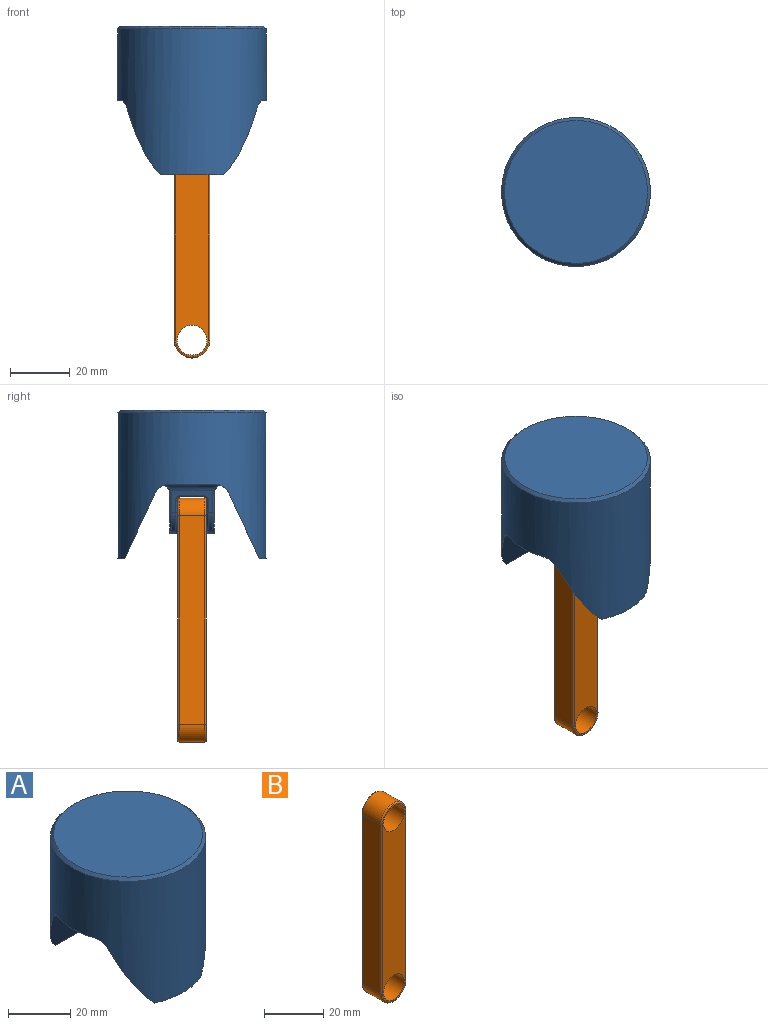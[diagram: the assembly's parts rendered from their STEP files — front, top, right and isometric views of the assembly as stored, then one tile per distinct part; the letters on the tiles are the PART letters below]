
ASSEMBLY  parts=2 mates=1
PART A: 54 faces, bbox 50x50x50 mm
  f0: plane 14.31x7.44mm, normal (-0.96,0,-0.29), area 44.3mm2, adj f1,f15,f22,f35,f36,f37,f38,f39
  f1: cylinder r=10mm len=19.11mm, axis (0,1,0), area 38.2mm2, adj f0,f2,f34,f43
  f2: plane 14.31x7.44mm, normal (0.96,0,-0.29), area 44.3mm2, adj f1,f15,f19,f28,f29,f30,f31,f32
  f3: cylinder r=5mm len=10mm, axis (0,1,0), area 78.5mm2, adj f18,f27
  f4: plane 15.65x10.28mm, normal (0,0,-1), area 154.5mm2, adj f6,f9,f11,f22
  f5: plane 21.08x2.33mm, normal (0,0,-1), area 33.1mm2, adj f6,f12
  f6: cylinder r=25mm len=50mm, axis (0,0,-1), area 5814.1mm2, adj f4,f5,f8,f9,f10,f11,f12,f13
  f7: plane 48x48mm, normal (0,0,1), area 1809.6mm2, adj f14
  f8: plane 21.08x2.33mm, normal (0,0,-1), area 33.1mm2, adj f6,f13
  f9: cylinder r=5mm len=47.49mm, axis (-1,0,0), area 214.5mm2, adj f4,f6,f10,f12,f19,f21,f22,f40
  f10: plane 15.65x10.28mm, normal (0,0,-1), area 154.5mm2, adj f6,f9,f11,f19
  f11: cylinder r=5mm len=47.49mm, axis (-1,0,0), area 214.5mm2, adj f4,f6,f10,f13,f19,f20,f22,f47
  f12: plane 43.47x22.11mm, normal (0,-0.91,-0.42), area 844.7mm2, adj f5,f6,f9
  f13: plane 43.47x22.11mm, normal (0,0.91,-0.42), area 844.7mm2, adj f6,f8,f11
  f14: cone r=24mm half-angle=45deg, axis (0,0,-1), area 217.7mm2, adj f6,f7
  f15: cylinder r=10mm len=19.11mm, axis (0,1,0), area 38.2mm2, adj f0,f2,f33,f50
  f16: cylinder r=5mm len=10mm, axis (0,1,0), area 78.5mm2, adj f17,f26
  f17: plane 22.11x13.11mm, normal (0,-1,0), area 139.9mm2, adj f16,f20,f49,f50,f51
  f18: plane 22.11x13.11mm, normal (0,1,0), area 139.9mm2, adj f3,f21,f42,f43,f44
  f19: cylinder r=3mm len=18.47mm, axis (0,1,0), area 63.3mm2, adj f2,f9,f10,f11,f40,f47
  f20: cylinder r=3mm len=26.72mm, axis (1,0,0), area 85mm2, adj f11,f17,f47,f48,f52,f53
  f21: cylinder r=3mm len=26.72mm, axis (-1,0,0), area 85mm2, adj f9,f18,f40,f41,f45,f46
  f22: cylinder r=3mm len=18.47mm, axis (0,-1,0), area 63.3mm2, adj f0,f4,f9,f11,f46,f53
  f23: cylinder r=1mm len=21.68mm, axis (-1,0,0), area 33.3mm2, adj f24,f27,f30,f38
  f24: plane 21.68x8mm, normal (0,0,-1), area 173.4mm2, adj f23,f25,f28,f39
  f25: cylinder r=1mm len=21.68mm, axis (-1,0,0), area 33.3mm2, adj f24,f26,f29,f37
  f26: plane 20.76x10.92mm, normal (0,1,0), area 93mm2, adj f16,f25,f31,f33,f35
  f27: plane 20.76x10.92mm, normal (0,-1,0), area 93mm2, adj f3,f23,f32,f34,f36
  f28: cylinder r=0.5mm len=8mm, axis (0,1,0), area 5.1mm2, adj f2,f24,f29,f30
  f29: bspline ~1.76x1.76mm, area 1.3mm2, adj f2,f25,f28,f31
  f30: bspline ~1.76x1.57mm, area 1.3mm2, adj f2,f23,f28,f32
  f31: cylinder r=0.5mm len=4.37mm, axis (0.29,0,0.96), area 3.5mm2, adj f2,f26,f29,f33
  f32: cylinder r=0.5mm len=4.37mm, axis (-0.29,0,-0.96), area 3.5mm2, adj f2,f27,f30,f34
  f33: torus R=9.5mm, axis (0,-1,0), area 19.6mm2, adj f15,f26,f31,f35
  f34: torus R=9.5mm, axis (0,-1,0), area 19.6mm2, adj f1,f27,f32,f36
  f35: cylinder r=0.5mm len=4.37mm, axis (0.29,0,-0.96), area 3.5mm2, adj f0,f26,f33,f37
  f36: cylinder r=0.5mm len=4.37mm, axis (-0.29,0,0.96), area 3.5mm2, adj f0,f27,f34,f38
  f37: bspline ~1.76x1.5mm, area 1.3mm2, adj f0,f25,f35,f39
  f38: bspline ~1.56x1.5mm, area 1.4mm2, adj f0,f23,f36,f39
  f39: cylinder r=0.5mm len=8mm, axis (0,-1,0), area 5.1mm2, adj f0,f24,f37,f38
  f40: bspline ~2.61x2.61mm, area 1.7mm2, adj f9,f19,f21,f41
  f41: bspline ~2.09x1.12mm, area 0.8mm2, adj f2,f21,f40,f42
  f42: cylinder r=0.5mm len=6.56mm, axis (0.29,0,0.96), area 5.3mm2, adj f2,f18,f41,f43
  f43: torus R=9.5mm, axis (0,-1,0), area 19.6mm2, adj f1,f18,f42,f44
  f44: cylinder r=0.5mm len=6.56mm, axis (0.29,0,-0.96), area 5.3mm2, adj f0,f18,f43,f45
  f45: bspline ~2.09x1.12mm, area 0.8mm2, adj f0,f21,f44,f46
  f46: bspline ~2.61x2.61mm, area 1.7mm2, adj f9,f21,f22,f45
  f47: bspline ~2.61x2.61mm, area 1.7mm2, adj f11,f19,f20,f48
  f48: bspline ~2.09x1.12mm, area 0.8mm2, adj f2,f20,f47,f49
  f49: cylinder r=0.5mm len=6.56mm, axis (-0.29,0,-0.96), area 5.3mm2, adj f2,f17,f48,f50
  f50: torus R=9.5mm, axis (0,-1,0), area 19.6mm2, adj f15,f17,f49,f51
  f51: cylinder r=0.5mm len=6.56mm, axis (-0.29,0,0.96), area 5.3mm2, adj f0,f17,f50,f52
  f52: bspline ~2.09x1.12mm, area 0.8mm2, adj f0,f20,f51,f53
  f53: bspline ~2.61x2.61mm, area 1.7mm2, adj f11,f20,f22,f52
PART B: 16 faces, bbox 13x9.5x83 mm
  f0: cylinder r=6mm len=12mm, axis (0,1,0), area 160.2mm2, adj f1,f3,f8,f12
  f1: plane 70x8.5mm, normal (-1,0,0), area 595mm2, adj f0,f2,f9,f13
  f2: cylinder r=6mm len=12mm, axis (0,1,0), area 160.2mm2, adj f1,f3,f11,f15
  f3: plane 70x8.5mm, normal (1,0,0), area 595mm2, adj f0,f2,f10,f14
  f4: cylinder r=5mm len=10mm, axis (0,1,0), area 298.5mm2, adj f6,f7
  f5: cylinder r=5mm len=10mm, axis (0,1,0), area 298.5mm2, adj f6,f7
  f6: plane 81x11mm, normal (0,-1,0), area 708mm2, adj f4,f5,f12,f13,f14,f15
  f7: plane 81x11mm, normal (0,1,0), area 708mm2, adj f4,f5,f8,f9,f10,f11
  f8: torus R=5.5mm, axis (0,-1,0), area 14.4mm2, adj f0,f7,f9,f10
  f9: cylinder r=0.5mm len=70mm, axis (0,0,-1), area 55mm2, adj f1,f7,f8,f11
  f10: cylinder r=0.5mm len=70mm, axis (0,0,1), area 55mm2, adj f3,f7,f8,f11
  f11: torus R=5.5mm, axis (0,-1,0), area 14.4mm2, adj f2,f7,f9,f10
  f12: torus R=5.5mm, axis (0,-1,0), area 14.4mm2, adj f0,f6,f13,f14
  f13: cylinder r=0.5mm len=70mm, axis (0,0,1), area 55mm2, adj f1,f6,f12,f15
  f14: cylinder r=0.5mm len=70mm, axis (0,0,-1), area 55mm2, adj f3,f6,f12,f15
  f15: torus R=5.5mm, axis (0,-1,0), area 14.4mm2, adj f2,f6,f13,f14
PLACE A t=(-25.07,-50.18,-49.96)mm
PLACE B t=(-25.07,-50.18,-49.96)mm
MATE revolute A.f3 <-> B.f0  axis (0,1,0) through (-25.07,-45.18,-60.53)mm
